# Revit family: Plumbing-Lavatories-Sloan-Valve-SS3001_
name_source: partatom
category: Plumbing Fixtures
units: mm (PartAtom-declared; Revit-internal decimal feet)

## family parameters
Cut with Voids When Loaded = Yes
Host = Face
OmniClass Number = 23.45.05.14.14
OmniClass Title = Sinks/Lavatories
Part Type = Normal
Room Calculation Point = No
Round Connector Dimension = Use Diameter
Shared = No

## types (3) — shared parameters
Assembly Code = D2010400
CWFU = 1.5
Cold Water Connection Diameter = 0"
Cold Water Connector Description = Cold Water Connector d3/8"
Default Elevation = 0"
Depth = 16 1/2"
Edition number = 1
HWFU = 1.5
Height = 7 1/2"
Hot Water Connection Diameter = 0"
Hot Water Connector Description = Hot Water Connector d3/8"
Keynote = 10000
Manufacturer = Sloan Valve
Product data url = https://bimobject.com
Sanitary Drain Connection Diameter = 1"
Sanitary Drain Connector Description = Sanitary Drain Connector d1 1/4"
URL = www.sloanvalve.com
Valve Pressure Drop = 0.00 psi
WFU = 2
Water Flow = 0 GPM
Width = 19 1/2"

## per-type parameters (varying)
| type | Description | Part Number | Product Material |
| SS-3001-CO | Carbon Offset, Vitreous China Undermount Lavatory | 3873001T | Sloan Valve - Vitreous China - White |
| SS-3001-STG | Vitreous China Undermount Lavatory with SloanTec® Glaze. | 3873071 | Sloan Valve - Vitreous China - SloanTec Glaze White |
| SS-3001 | Vitreous China Undermount Lavatory. | 3873001 | Sloan Valve - Vitreous China - White |

note: column(s) folded — value = type name in every type: Model

## geometry (parser evidence)
native form markers: Sweep x2
no freeform markers — native parametric forms only
